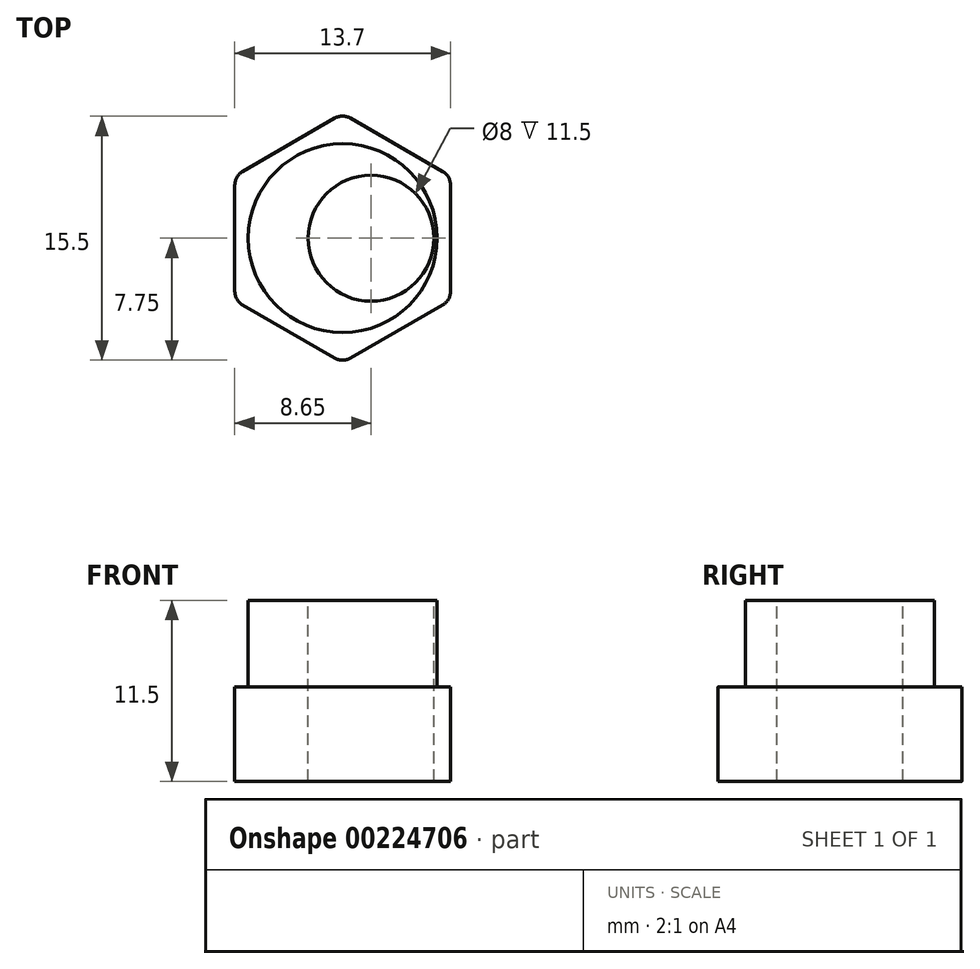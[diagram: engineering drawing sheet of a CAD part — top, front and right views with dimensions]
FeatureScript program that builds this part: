
annotation { "Feature Type Name" : "Feature", "Feature Type Description" : "" }
export const myFeature = defineFeature(function(context is Context, id is Id, definition is map)
    precondition{}
    {
        {
            var Q0;
            Q0=qCreatedBy(makeId("Top.planeOp"),FACE);
            var sketch = newSketch(context, id + "F0", { "sketchPlane" : qUnion([Q0])});
            skCircle(sketch, "E0.cCircle", {"center": v(0, 0) * mm, "radius": 6.85 * mm, "construction": true});
            skLineSegment(sketch, "E0.0", {"start": v(6.85, 3.95) * mm, "end": v(6.85, -3.95) * mm});
            skLineSegment(sketch, "E0.1", {"start": v(6.85, -3.95) * mm, "end": v(0, -7.9) * mm});
            skLineSegment(sketch, "E0.2", {"start": v(0, -7.9) * mm, "end": v(-6.85, -3.95) * mm});
            skLineSegment(sketch, "E0.3", {"start": v(-6.85, -3.95) * mm, "end": v(-6.85, 3.95) * mm});
            skLineSegment(sketch, "E0.4", {"start": v(-6.85, 3.95) * mm, "end": v(0, 7.9) * mm});
            skLineSegment(sketch, "E0.5", {"start": v(0, 7.9) * mm, "end": v(6.85, 3.95) * mm});
            skPoint(sketch, "E0.0.midPoint", {"position": v(6.85, 0) * mm});
            skSolve(sketch);
        }
        {
            var Q0;
            Q0=makeQuery(id+"F0.imprint","IMPRINT",FACE,{"disambiguationData":[TD([[makeQuery(id+"F0.imprint","IMPRINT",EDGE,{"derivedFrom":sQuery(id+"F0.wireOp",EDGE,"E0.0")}),-1.0]])]});
            extrude(context, id + "F1", {"entities" : qUnion([Q0]), "depth" : 6 * mm});
        }
        {
            var Q0;
            Q0=makeQuery(id+"F1.opExtrude","CAP_FACE",FACE,{"disambiguationData":[OSD([sQuery(id+"F0.wireOp",EDGE,"E0.0"),sQuery(id+"F0.wireOp",EDGE,"E0.1"),sQuery(id+"F0.wireOp",EDGE,"E0.2"),sQuery(id+"F0.wireOp",EDGE,"E0.3"),sQuery(id+"F0.wireOp",EDGE,"E0.4"),sQuery(id+"F0.wireOp",EDGE,"E0.5")])],"isStart":false});
            var sketch = newSketch(context, id + "F2", { "sketchPlane" : qUnion([Q0])});
            skCircle(sketch, "E1", {"center": v(0, 0) * mm, "radius": 6 * mm});
            skSolve(sketch);
        }
        {
            var Q0;
            Q0=makeQuery(id+"F2.imprint","IMPRINT",FACE,{"disambiguationData":[TD([[makeQuery(id+"F2.imprint","IMPRINT",EDGE,{"derivedFrom":sQuery(id+"F2.wireOp",EDGE,"E1")}),1.0]])]});
            extrude(context, id + "F3", {"entities" : qUnion([Q0]), "operationType" : NewBodyOperationType.ADD, "depth" : 5.5 * mm});
        }
        {
            var Q0;
            Q0=makeQuery(id+"F3.opExtrude","CAP_FACE",FACE,{"disambiguationData":[OSD([sQuery(id+"F2.wireOp",EDGE,"E1")])],"isStart":false});
            var sketch = newSketch(context, id + "F4", { "sketchPlane" : qUnion([Q0])});
            skCircle(sketch, "E2", {"center": v(1.8, 0) * mm, "radius": 4 * mm});
            skSolve(sketch);
        }
        {
            var Q0;
            Q0=makeQuery(id+"F4.imprint","IMPRINT",FACE,{"disambiguationData":[TD([[makeQuery(id+"F4.imprint","IMPRINT",EDGE,{"derivedFrom":sQuery(id+"F4.wireOp",EDGE,"E2")}),1.0]])]});
            extrude(context, id + "F5", {"entities" : qUnion([Q0]), "operationType" : NewBodyOperationType.REMOVE, "endBound" : BoundingType.THROUGH_ALL, "oppositeDirection" : true, "depth" : 25 * mm});
        }
        {
            var Q0;
            Q0=makeQuery(id+"F1.opExtrude","SWEPT_EDGE",EDGE,{"disambiguationData":[OSD([sQuery(id+"F0.wireOp",EDGE,"E0.0"),sQuery(id+"F0.wireOp",EDGE,"E0.1")])]});
            var Q1;
            Q1=makeQuery(id+"F1.opExtrude","SWEPT_EDGE",EDGE,{"disambiguationData":[OSD([sQuery(id+"F0.wireOp",EDGE,"E0.1"),sQuery(id+"F0.wireOp",EDGE,"E0.2")])]});
            var Q2;
            Q2=makeQuery(id+"F1.opExtrude","SWEPT_EDGE",EDGE,{"disambiguationData":[OSD([sQuery(id+"F0.wireOp",EDGE,"E0.0"),sQuery(id+"F0.wireOp",EDGE,"E0.5")])]});
            var Q3;
            Q3=makeQuery(id+"F1.opExtrude","SWEPT_EDGE",EDGE,{"disambiguationData":[OSD([sQuery(id+"F0.wireOp",EDGE,"E0.2"),sQuery(id+"F0.wireOp",EDGE,"E0.3")])]});
            var Q4;
            Q4=makeQuery(id+"F1.opExtrude","SWEPT_EDGE",EDGE,{"disambiguationData":[OSD([sQuery(id+"F0.wireOp",EDGE,"E0.3"),sQuery(id+"F0.wireOp",EDGE,"E0.4")])]});
            var Q5;
            Q5=makeQuery(id+"F1.opExtrude","SWEPT_EDGE",EDGE,{"disambiguationData":[OSD([sQuery(id+"F0.wireOp",EDGE,"E0.4"),sQuery(id+"F0.wireOp",EDGE,"E0.5")])]});
            fillet(context, id + "F6", {"entities" : qUnion([Q0, Q1, Q2, Q3, Q4, Q5]), "radius" : 1 * mm, "tangentPropagation" : true, "allowEdgeOverflow" : false});
        }
    });
